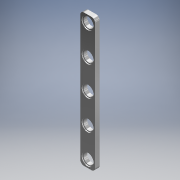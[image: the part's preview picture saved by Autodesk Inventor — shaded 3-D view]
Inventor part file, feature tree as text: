
AUTODESK INVENTOR PART (.ipt)
format: ipt  version: 2016 (Build 200138000, 138)  size: 161,792 bytes
history: native  units: mm (DEFAULTED — no unit token found)
features: extrude x3, fillet x2, sketch x1
ambient origin geometry x8: Origin, YZ Plane, XZ Plane, XY Plane, X Axis, Y Axis, Z Axis, Center Point
bodies: Solid1 (feature_tree)
feature tree (6):
  extrude  "Stock Block"  Depth=228.6mm
  extrude  "Bearing Flange Cutout"  Depth=6.35mm
  fillet  "Fillet4"  Radius=12.7mm
  extrude  "Weight Savings Bro"  Depth=7.9375mm TaperAngle=0.0deg
  fillet  "Fillet3"  Radius=25.4mm
  sketch  "Sketch2"  dims[d0=25.4mm d1=228.6mm d2=17.4625mm d3=12.7mm d4=7.9375mm d5=0.0mm d8=25.4mm d9=0.0mm d14=20.6375mm d17=1.5875mm d18=0.0mm d40=17.4625mm d41=12.7mm d42=12.7mm d46=25.4mm d47=6.35mm d49=25.4mm d50=6.35mm d51=20.6375mm d54=6.35mm d55=25.4mm d56=25.4mm d57=50.8mm d58=12.7mm d59=50.8mm d60=6.35mm]
